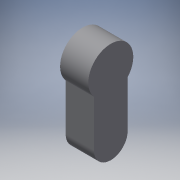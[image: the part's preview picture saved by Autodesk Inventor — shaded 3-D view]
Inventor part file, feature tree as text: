
AUTODESK INVENTOR PART (.ipt)
format: ipt  version: 2017 (Build 210142000, 142)  size: 148,480 bytes
history: native  units: in
note: dims shown in document units (in); Inventor stores cm internally (conversion verified against a paired STEP export)
features: extrude x3, sketch x3, projected_geometry x3
ambient origin geometry x8: Origin, YZ Plane, XZ Plane, XY Plane, X Axis, Y Axis, Z Axis, Center Point
bodies: Solid1 (feature_tree)
feature tree (9):
  extrude  "Extrusion1"  Depth=1.18in
  extrude  "Extrusion2"  Depth=0.985in TaperAngle=0.0deg
  extrude  "Extrusion3"  Depth=0.0325in
  sketch  "Sketch1"  dims[d0=1.57in d1=1.18in]
  sketch  "Sketch2"  dims[d2=3.52in d3=0.985in d4=0.0in]
  projected_geometry  "Projected Loop1"
  sketch  "Sketch3"  dims[d5=0.2075in d6=0.0325in d7=1.58in d8=1.0in d9=0.466in d10=0.0in d11=0.0885in d12=0.064in d13=0.064in d14=0.033in d15=0.0595in d16=0.09in d17=0.0885in d18=0.087in d19=0.466in d20=0.0in]
  projected_geometry  "Projected Loop2"
  projected_geometry  "Projected Loop3"
